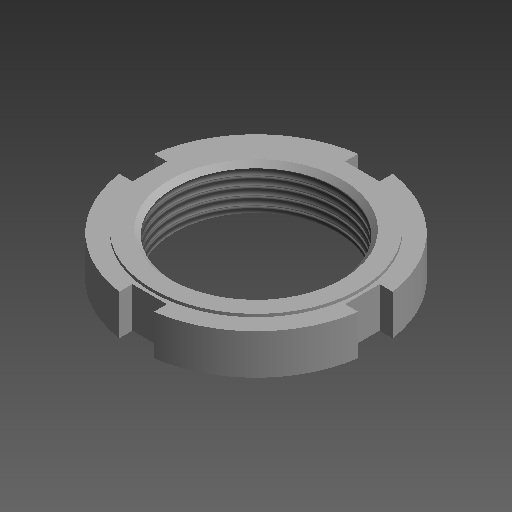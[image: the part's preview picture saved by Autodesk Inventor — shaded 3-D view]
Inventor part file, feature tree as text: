
AUTODESK INVENTOR PART (.ipt)
format: ipt  version: 2021 (Build 250183000, 183)  size: 159,232 bytes
history: native  units: mm (DEFAULTED — no unit token found)
features: other x14, sketch x4, revolve x3, thread x1, extrude x1
ambient origin geometry x8: Origin, YZ Plane, XZ Plane, XY Plane, X Axis, Y Axis, Z Axis, Center Point
bodies: Solid1 (feature_tree)
feature tree (23):
  revolve  "Revolution1"  Angle=360.0deg
  revolve  "Revolution2"  Angle=360.0deg
  thread  "Thread1"  [1 undecoded]
  revolve  "Revolution3"  [1 undecoded]
  extrude  "Extrusion1"  [1 undecoded]
  other  "FDT_CYLINDER_XY"
  other  "FDT_CYLINDER_YZ"
  other  "FDT_CYLINDER_ZX"
  other  "FDT_CYLINDER_X"
  other  "FDT_CYLINDER_Y"
  other  "FDT_CYLINDER_Z"
  other  "FDT_CYLINDER_Center"
  other  "NUT_XY"
  other  "NUT_YZ"
  other  "NUT_ZX"
  other  "NUT_X"
  other  "NUT_Y"
  other  "NUT_Z"
  other  "NUT_Center"
  sketch  "Sketch_1"  dims[d0=360.0deg d1=360.0deg]
  sketch  "Sketch_2"  dims[d2=6.71919mm d3=0.0mm d4=360.0deg d5=8.0mm d6=0.0mm]
  sketch  "Sketch_6"
  sketch  "Sketch_3"  dims[d7=0.0mm d8=0.0mm]
note: 3 required parameter values undecoded (feature->parameter linkage not recoverable at this tier; creation-order binding heuristic only, values carry confidence <= 0.55)